# Revit family: ВУТ_ВУЕ ПБЕ_В_Л_П_Eng
name_source: partatom
category: Mechanical Equipment
units: mm (PartAtom-declared; Revit-internal decimal feet)

## family parameters
Always vertical = Yes
Classification = None
Cut with Voids When Loaded = No
Part Type = Normal
Room Calculation Point = No
Round Connector Dimension = Use Diameter
Shared = No
Work Plane-Based = No

## types (24) — shared parameters
00_20_Manufacturer = Vents
00_20_Name = Air handling units with heat recovery
Casing Material = Steel, galvanized
Filter = G4
Frequency = 50 Hz
Load Classification = HVAC
Maintenance zone material = <By Category>
Manufacturer = Vents
URL = https://ventilation-system.com
zero-valued in all types: Default Elevation

## per-type parameters (varying)
- VUE 300 PBE  ЕС L А21 DTV: 2000=No; 2000 PBV=No; Amperage=8 A; Apparent Load=1817 VA; B=485 mm; B3=135 mm  [stored 0.442913 ft]; B31=350 mm  [stored 1.14829 ft]; DW=12 mm  [stored 0.0393701 ft]; Diameter=160 mm  [stored 0.524934 ft]; Dn=155 mm  [stored 0.50853 ft]; Dy=160 mm  [stored 0.524934 ft]; EB=510 mm; EB1=268 mm  [stored 0.879265 ft]; EB2=50 mm  [stored 0.164042 ft]; H=280 mm  [stored 0.918635 ft]; H1=129 mm  [stored 0.423228 ft]; H2=590 mm; HW1=120 mm  [stored 0.393701 ft]; HW2=273 mm; Height=280 mm  [stored 0.918635 ft]; L=1238 mm; L1=1291 mm; LW1=254 mm; LW2=219 mm; Left=Yes; Left PBV=No; Left preostat=Yes; Length=1291 mm; Maximum Air Flow=340.0 m³/h; Number of Fase=1; Power=1680 W; Right=No; Right PBV=No; Sound pressure level at 3 m distance=27 dBA; Voltage=230 V; Weight=44.00 kg; Width=485 mm; b=243 mm
- VUT 300 PBE  ЕС L А21 DTV: 2000=No; 2000 PBV=No; Amperage=8 A; Apparent Load=1817 VA; B=485 mm; B3=135 mm  [stored 0.442913 ft]; B31=350 mm  [stored 1.14829 ft]; DW=12 mm  [stored 0.0393701 ft]; Diameter=160 mm  [stored 0.524934 ft]; Dn=155 mm  [stored 0.50853 ft]; Dy=160 mm  [stored 0.524934 ft]; EB=510 mm; EB1=268 mm  [stored 0.879265 ft]; EB2=50 mm  [stored 0.164042 ft]; H=280 mm  [stored 0.918635 ft]; H1=129 mm  [stored 0.423228 ft]; H2=590 mm; HW1=120 mm  [stored 0.393701 ft]; HW2=273 mm; Height=280 mm  [stored 0.918635 ft]; L=1238 mm; L1=1291 mm; LW1=254 mm; LW2=219 mm; Left=Yes; Left PBV=No; Left preostat=Yes; Length=1291 mm; Maximum Air Flow=340.0 m³/h; Number of Fase=1; Power=1680 W; Right=No; Right PBV=No; Sound pressure level at 3 m distance=27 dBA; Voltage=230 V; Weight=44.00 kg; Width=485 mm; b=243 mm
- VUE 300 PBE  ЕС R А21 DTV: 2000=No; 2000 PBV=No; Amperage=8 A; Apparent Load=1817 VA; B=485 mm; B3=350 mm  [stored 1.14829 ft]; B31=135 mm  [stored 0.442913 ft]; DW=12 mm  [stored 0.0393701 ft]; Diameter=160 mm  [stored 0.524934 ft]; Dn=155 mm  [stored 0.50853 ft]; Dy=160 mm  [stored 0.524934 ft]; EB=510 mm; EB1=268 mm  [stored 0.879265 ft]; EB2=50 mm  [stored 0.164042 ft]; H=280 mm  [stored 0.918635 ft]; H1=129 mm  [stored 0.423228 ft]; H2=590 mm; HW1=120 mm  [stored 0.393701 ft]; HW2=273 mm; Height=280 mm  [stored 0.918635 ft]; L=1238 mm; L1=1291 mm; LW1=254 mm; LW2=219 mm; Left=No; Left PBV=No; Left preostat=Yes; Length=1291 mm; Maximum Air Flow=340.0 m³/h; Number of Fase=1; Power=1680 W; Right=Yes; Right PBV=No; Sound pressure level at 3 m distance=27 dBA; Voltage=230 V; Weight=44.00 kg; Width=485 mm; b=243 mm
- VUT 300 PBE  ЕС R А21 DTV: 2000=No; 2000 PBV=No; Amperage=8 A; Apparent Load=1817 VA; B=485 mm; B3=350 mm  [stored 1.14829 ft]; B31=135 mm  [stored 0.442913 ft]; DW=12 mm  [stored 0.0393701 ft]; Diameter=160 mm  [stored 0.524934 ft]; Dn=155 mm  [stored 0.50853 ft]; Dy=160 mm  [stored 0.524934 ft]; EB=510 mm; EB1=268 mm  [stored 0.879265 ft]; EB2=50 mm  [stored 0.164042 ft]; H=280 mm  [stored 0.918635 ft]; H1=129 mm  [stored 0.423228 ft]; H2=590 mm; HW1=120 mm  [stored 0.393701 ft]; HW2=273 mm; Height=280 mm  [stored 0.918635 ft]; L=1238 mm; L1=1291 mm; LW1=254 mm; LW2=219 mm; Left=No; Left PBV=No; Left preostat=Yes; Length=1291 mm; Maximum Air Flow=340.0 m³/h; Number of Fase=1; Power=1680 W; Right=Yes; Right PBV=No; Sound pressure level at 3 m distance=27 dBA; Voltage=230 V; Weight=44.00 kg; Width=485 mm; b=243 mm
- VUE 550 PBE  ЕС L А21 DTV: 2000=No; 2000 PBV=No; Amperage=11 A; Apparent Load=2553 VA; B=827 mm; B3=188 mm  [stored 0.616798 ft]; B31=639 mm; DW=12 mm  [stored 0.0393701 ft]; Diameter=200 mm  [stored 0.656168 ft]; Dn=195 mm  [stored 0.639764 ft]; Dy=200 mm  [stored 0.656168 ft]; EB=802 mm; EB1=389 mm; EB2=5 mm  [stored 0.0164042 ft]; H=280 mm  [stored 0.918635 ft]; H1=120 mm  [stored 0.393701 ft]; H2=590 mm; HW1=160 mm  [stored 0.524934 ft]; HW2=250 mm  [stored 0.82021 ft]; Height=280 mm  [stored 0.918635 ft]; L=1238 mm; L1=1291 mm; LW1=350 mm  [stored 1.14829 ft]; LW2=370 mm  [stored 1.21391 ft]; Left=Yes; Left PBV=No; Left preostat=Yes; Length=1291 mm; Maximum Air Flow=620.0 m³/h; Number of Fase=1; Power=2297 W; Right=No; Right PBV=No; Sound pressure level at 3 m distance=30 dBA; Voltage=230 V; Weight=67.00 kg; Width=827 mm; b=414 mm
- VUE 550 PBE  ЕС R А21 DTV: 2000=No; 2000 PBV=No; Amperage=11 A; Apparent Load=2553 VA; B=827 mm; B3=188 mm  [stored 0.616798 ft]; B31=639 mm; DW=12 mm  [stored 0.0393701 ft]; Diameter=200 mm  [stored 0.656168 ft]; Dn=195 mm  [stored 0.639764 ft]; Dy=200 mm  [stored 0.656168 ft]; EB=802 mm; EB1=389 mm; EB2=5 mm  [stored 0.0164042 ft]; H=280 mm  [stored 0.918635 ft]; H1=120 mm  [stored 0.393701 ft]; H2=590 mm; HW1=160 mm  [stored 0.524934 ft]; HW2=250 mm  [stored 0.82021 ft]; Height=280 mm  [stored 0.918635 ft]; L=1238 mm; L1=1291 mm; LW1=350 mm  [stored 1.14829 ft]; LW2=370 mm  [stored 1.21391 ft]; Left=No; Left PBV=No; Left preostat=Yes; Length=1291 mm; Maximum Air Flow=620.0 m³/h; Number of Fase=1; Power=2297 W; Right=Yes; Right PBV=No; Sound pressure level at 3 m distance=30 dBA; Voltage=230 V; Weight=67.00 kg; Width=827 mm; b=414 mm
- VUT 550 PBE  ЕС L А21 DTV: 2000=No; 2000 PBV=No; Amperage=11 A; Apparent Load=2553 VA; B=827 mm; B3=188 mm  [stored 0.616798 ft]; B31=639 mm; DW=12 mm  [stored 0.0393701 ft]; Diameter=200 mm  [stored 0.656168 ft]; Dn=195 mm  [stored 0.639764 ft]; Dy=200 mm  [stored 0.656168 ft]; EB=802 mm; EB1=389 mm; EB2=5 mm  [stored 0.0164042 ft]; H=280 mm  [stored 0.918635 ft]; H1=120 mm  [stored 0.393701 ft]; H2=590 mm; HW1=160 mm  [stored 0.524934 ft]; HW2=250 mm  [stored 0.82021 ft]; Height=280 mm  [stored 0.918635 ft]; L=1238 mm; L1=1291 mm; LW1=350 mm  [stored 1.14829 ft]; LW2=370 mm  [stored 1.21391 ft]; Left=Yes; Left PBV=No; Left preostat=Yes; Length=1291 mm; Maximum Air Flow=620.0 m³/h; Number of Fase=1; Power=2297 W; Right=No; Right PBV=No; Sound pressure level at 3 m distance=30 dBA; Voltage=230 V; Weight=67.00 kg; Width=827 mm; b=414 mm
- VUT 550 PBE  ЕС R А21 DTV: 2000=No; 2000 PBV=No; Amperage=11 A; Apparent Load=2553 VA; B=827 mm; B3=188 mm  [stored 0.616798 ft]; B31=639 mm; DW=12 mm  [stored 0.0393701 ft]; Diameter=200 mm  [stored 0.656168 ft]; Dn=195 mm  [stored 0.639764 ft]; Dy=200 mm  [stored 0.656168 ft]; EB=802 mm; EB1=389 mm; EB2=5 mm  [stored 0.0164042 ft]; H=280 mm  [stored 0.918635 ft]; H1=120 mm  [stored 0.393701 ft]; H2=590 mm; HW1=160 mm  [stored 0.524934 ft]; HW2=250 mm  [stored 0.82021 ft]; Height=280 mm  [stored 0.918635 ft]; L=1238 mm; L1=1291 mm; LW1=350 mm  [stored 1.14829 ft]; LW2=370 mm  [stored 1.21391 ft]; Left=No; Left PBV=No; Left preostat=Yes; Length=1291 mm; Maximum Air Flow=620.0 m³/h; Number of Fase=1; Power=2297 W; Right=Yes; Right PBV=No; Sound pressure level at 3 m distance=30 dBA; Voltage=230 V; Weight=67.00 kg; Width=827 mm; b=414 mm
- VUE 900 PBE  ЕС L А21 DTV: 2000=No; 2000 PBV=No; Amperage=17 A; Apparent Load=4002 VA; B=1351 mm; B3=350 mm  [stored 1.14829 ft]; B31=1080 mm; DW=20 mm  [stored 0.0656168 ft]; Diameter=250 mm  [stored 0.82021 ft]; Dn=245 mm  [stored 0.803806 ft]; Dy=250 mm  [stored 0.82021 ft]; EB=1326 mm; EB1=651 mm; EB2=5 mm  [stored 0.0164042 ft]; H=318 mm  [stored 1.04331 ft]; H1=143 mm; H2=590 mm; HW1=50 mm  [stored 0.164042 ft]; HW2=265 mm  [stored 0.869423 ft]; Height=318 mm  [stored 1.04331 ft]; L=1349 mm; L1=1402 mm; LW1=70 mm  [stored 0.229659 ft]; LW2=135 mm  [stored 0.442913 ft]; Left=Yes; Left PBV=No; Left preostat=Yes; Length=1402 mm; Maximum Air Flow=1030.0 m³/h; Number of Fase=1; Power=3742 W; Right=No; Right PBV=No; Sound pressure level at 3 m distance=33 dBA; Voltage=230 V; Weight=111.00 kg; Width=1351 mm; b=676 mm
- VUE 900 PBE  ЕС R А21 DTV: 2000=No; 2000 PBV=No; Amperage=17 A; Apparent Load=4002 VA; B=1351 mm; B3=430 mm; B31=1080 mm; DW=20 mm  [stored 0.0656168 ft]; Diameter=250 mm  [stored 0.82021 ft]; Dn=245 mm  [stored 0.803806 ft]; Dy=250 mm  [stored 0.82021 ft]; EB=1326 mm; EB1=651 mm; EB2=5 mm  [stored 0.0164042 ft]; H=318 mm  [stored 1.04331 ft]; H1=143 mm; H2=590 mm; HW1=50 mm  [stored 0.164042 ft]; HW2=265 mm  [stored 0.869423 ft]; Height=318 mm  [stored 1.04331 ft]; L=1349 mm; L1=1402 mm; LW1=70 mm  [stored 0.229659 ft]; LW2=135 mm  [stored 0.442913 ft]; Left=No; Left PBV=No; Left preostat=Yes; Length=1402 mm; Maximum Air Flow=1030.0 m³/h; Number of Fase=1; Power=3742 W; Right=Yes; Right PBV=No; Sound pressure level at 3 m distance=33 dBA; Voltage=230 V; Weight=111.00 kg; Width=1351 mm; b=676 mm
- VUT 900 PBE  ЕС L А21 DTV: 2000=No; 2000 PBV=No; Amperage=17 A; Apparent Load=4002 VA; B=1351 mm; B3=350 mm  [stored 1.14829 ft]; B31=1080 mm; DW=20 mm  [stored 0.0656168 ft]; Diameter=250 mm  [stored 0.82021 ft]; Dn=245 mm  [stored 0.803806 ft]; Dy=250 mm  [stored 0.82021 ft]; EB=1326 mm; EB1=651 mm; EB2=5 mm  [stored 0.0164042 ft]; H=318 mm  [stored 1.04331 ft]; H1=143 mm; H2=590 mm; HW1=50 mm  [stored 0.164042 ft]; HW2=265 mm  [stored 0.869423 ft]; Height=318 mm  [stored 1.04331 ft]; L=1349 mm; L1=1402 mm; LW1=70 mm  [stored 0.229659 ft]; LW2=135 mm  [stored 0.442913 ft]; Left=Yes; Left PBV=No; Left preostat=Yes; Length=1402 mm; Maximum Air Flow=1030.0 m³/h; Number of Fase=1; Power=3742 W; Right=No; Right PBV=No; Sound pressure level at 3 m distance=33 dBA; Voltage=230 V; Weight=111.00 kg; Width=1351 mm; b=676 mm
- VUT 900 PBE  ЕС R А21 DTV: 2000=No; 2000 PBV=No; Amperage=17 A; Apparent Load=4002 VA; B=1351 mm; B3=430 mm; B31=1080 mm; DW=20 mm  [stored 0.0656168 ft]; Diameter=250 mm  [stored 0.82021 ft]; Dn=245 mm  [stored 0.803806 ft]; Dy=250 mm  [stored 0.82021 ft]; EB=1326 mm; EB1=651 mm; EB2=5 mm  [stored 0.0164042 ft]; H=318 mm  [stored 1.04331 ft]; H1=143 mm; H2=590 mm; HW1=50 mm  [stored 0.164042 ft]; HW2=265 mm  [stored 0.869423 ft]; Height=318 mm  [stored 1.04331 ft]; L=1349 mm; L1=1402 mm; LW1=70 mm  [stored 0.229659 ft]; LW2=135 mm  [stored 0.442913 ft]; Left=No; Left PBV=No; Left preostat=Yes; Length=1402 mm; Maximum Air Flow=1030.0 m³/h; Number of Fase=1; Power=3742 W; Right=Yes; Right PBV=No; Sound pressure level at 3 m distance=33 dBA; Voltage=230 V; Weight=111.00 kg; Width=1351 mm; b=676 mm
- VUE 550 PBW ЕС L А21 DTV: 2000=No; 2000 PBV=No; Amperage=2 A; Apparent Load=552 VA; B=827 mm; B3=188 mm  [stored 0.616798 ft]; B31=639 mm; DW=12 mm  [stored 0.0393701 ft]; Diameter=200 mm  [stored 0.656168 ft]; Dn=195 mm  [stored 0.639764 ft]; Dy=200 mm  [stored 0.656168 ft]; EB=802 mm; EB1=389 mm; EB2=5 mm  [stored 0.0164042 ft]; H=280 mm  [stored 0.918635 ft]; H1=120 mm  [stored 0.393701 ft]; H2=590 mm; HW1=160 mm  [stored 0.524934 ft]; HW2=250 mm  [stored 0.82021 ft]; Height=280 mm  [stored 0.918635 ft]; L=1238 mm; L1=1291 mm; LW1=350 mm  [stored 1.14829 ft]; LW2=370 mm  [stored 1.21391 ft]; Left=Yes; Left PBV=Yes; Left preostat=Yes; Length=1291 mm; Maximum Air Flow=620.0 m³/h; Number of Fase=1; Power=297 W; Right=No; Right PBV=No; Sound pressure level at 3 m distance=30 dBA; Voltage=230 V; Weight=68.00 kg; Width=827 mm; b=414 mm
- VUT 550 PBW ЕС L А21 DTV: 2000=No; 2000 PBV=No; Amperage=2 A; Apparent Load=552 VA; B=827 mm; B3=188 mm  [stored 0.616798 ft]; B31=639 mm; DW=12 mm  [stored 0.0393701 ft]; Diameter=200 mm  [stored 0.656168 ft]; Dn=195 mm  [stored 0.639764 ft]; Dy=200 mm  [stored 0.656168 ft]; EB=802 mm; EB1=389 mm; EB2=5 mm  [stored 0.0164042 ft]; H=280 mm  [stored 0.918635 ft]; H1=120 mm  [stored 0.393701 ft]; H2=590 mm; HW1=160 mm  [stored 0.524934 ft]; HW2=250 mm  [stored 0.82021 ft]; Height=280 mm  [stored 0.918635 ft]; L=1238 mm; L1=1291 mm; LW1=350 mm  [stored 1.14829 ft]; LW2=370 mm  [stored 1.21391 ft]; Left=Yes; Left PBV=Yes; Left preostat=Yes; Length=1291 mm; Maximum Air Flow=620.0 m³/h; Number of Fase=1; Power=297 W; Right=No; Right PBV=No; Sound pressure level at 3 m distance=30 dBA; Voltage=230 V; Weight=68.00 kg; Width=827 mm; b=414 mm
- VUE 550 PBW ЕС R А21 DTV: 2000=No; 2000 PBV=No; Amperage=2 A; Apparent Load=552 VA; B=827 mm; B3=188 mm  [stored 0.616798 ft]; B31=639 mm; DW=12 mm  [stored 0.0393701 ft]; Diameter=200 mm  [stored 0.656168 ft]; Dn=195 mm  [stored 0.639764 ft]; Dy=200 mm  [stored 0.656168 ft]; EB=802 mm; EB1=389 mm; EB2=5 mm  [stored 0.0164042 ft]; H=280 mm  [stored 0.918635 ft]; H1=120 mm  [stored 0.393701 ft]; H2=590 mm; HW1=160 mm  [stored 0.524934 ft]; HW2=250 mm  [stored 0.82021 ft]; Height=280 mm  [stored 0.918635 ft]; L=1238 mm; L1=1291 mm; LW1=350 mm  [stored 1.14829 ft]; LW2=370 mm  [stored 1.21391 ft]; Left=No; Left PBV=No; Left preostat=Yes; Length=1291 mm; Maximum Air Flow=620.0 m³/h; Number of Fase=1; Power=297 W; Right=Yes; Right PBV=Yes; Sound pressure level at 3 m distance=30 dBA; Voltage=230 V; Weight=68.00 kg; Width=827 mm; b=414 mm
- VUT 550 PBW ЕС R А21 DTV: 2000=No; 2000 PBV=No; Amperage=2 A; Apparent Load=552 VA; B=827 mm; B3=188 mm  [stored 0.616798 ft]; B31=639 mm; DW=12 mm  [stored 0.0393701 ft]; Diameter=200 mm  [stored 0.656168 ft]; Dn=195 mm  [stored 0.639764 ft]; Dy=200 mm  [stored 0.656168 ft]; EB=802 mm; EB1=389 mm; EB2=5 mm  [stored 0.0164042 ft]; H=280 mm  [stored 0.918635 ft]; H1=120 mm  [stored 0.393701 ft]; H2=590 mm; HW1=160 mm  [stored 0.524934 ft]; HW2=250 mm  [stored 0.82021 ft]; Height=280 mm  [stored 0.918635 ft]; L=1238 mm; L1=1291 mm; LW1=350 mm  [stored 1.14829 ft]; LW2=370 mm  [stored 1.21391 ft]; Left=No; Left PBV=No; Left preostat=Yes; Length=1291 mm; Maximum Air Flow=620.0 m³/h; Number of Fase=1; Power=297 W; Right=Yes; Right PBV=Yes; Sound pressure level at 3 m distance=30 dBA; Voltage=230 V; Weight=68.00 kg; Width=827 mm; b=414 mm
- VUE 900 PBW ЕС L А21 DTV: 2000=No; 2000 PBV=No; Amperage=3 A; Apparent Load=690 VA; B=1351 mm; B3=350 mm  [stored 1.14829 ft]; B31=1080 mm; DW=20 mm  [stored 0.0656168 ft]; Diameter=250 mm  [stored 0.82021 ft]; Dn=245 mm  [stored 0.803806 ft]; Dy=250 mm  [stored 0.82021 ft]; EB=1326 mm; EB1=651 mm; EB2=5 mm  [stored 0.0164042 ft]; H=318 mm  [stored 1.04331 ft]; H1=143 mm; H2=590 mm; HW1=50 mm  [stored 0.164042 ft]; HW2=265 mm  [stored 0.869423 ft]; Height=318 mm  [stored 1.04331 ft]; L=1349 mm; L1=1402 mm; LW1=70 mm  [stored 0.229659 ft]; LW2=135 mm  [stored 0.442913 ft]; Left=Yes; Left PBV=Yes; Left preostat=Yes; Length=1402 mm; Maximum Air Flow=1030.0 m³/h; Number of Fase=1; Power=442 W; Right=No; Right PBV=No; Sound pressure level at 3 m distance=33 dBA; Voltage=230 V; Weight=112.00 kg; Width=1351 mm; b=676 mm
- VUT 900 PBW ЕС L А21 DTV: 2000=No; 2000 PBV=No; Amperage=3 A; Apparent Load=690 VA; B=1351 mm; B3=350 mm  [stored 1.14829 ft]; B31=1080 mm; DW=20 mm  [stored 0.0656168 ft]; Diameter=250 mm  [stored 0.82021 ft]; Dn=245 mm  [stored 0.803806 ft]; Dy=250 mm  [stored 0.82021 ft]; EB=1326 mm; EB1=651 mm; EB2=5 mm  [stored 0.0164042 ft]; H=318 mm  [stored 1.04331 ft]; H1=143 mm; H2=590 mm; HW1=50 mm  [stored 0.164042 ft]; HW2=265 mm  [stored 0.869423 ft]; Height=318 mm  [stored 1.04331 ft]; L=1349 mm; L1=1402 mm; LW1=70 mm  [stored 0.229659 ft]; LW2=135 mm  [stored 0.442913 ft]; Left=Yes; Left PBV=Yes; Left preostat=Yes; Length=1402 mm; Maximum Air Flow=1030.0 m³/h; Number of Fase=1; Power=442 W; Right=No; Right PBV=No; Sound pressure level at 3 m distance=33 dBA; Voltage=230 V; Weight=112.00 kg; Width=1351 mm; b=676 mm
- VUE 900 PBW ЕС R А21 DTV: 2000=No; 2000 PBV=No; Amperage=3 A; Apparent Load=690 VA; B=1351 mm; B3=430 mm; B31=1080 mm; DW=20 mm  [stored 0.0656168 ft]; Diameter=250 mm  [stored 0.82021 ft]; Dn=245 mm  [stored 0.803806 ft]; Dy=250 mm  [stored 0.82021 ft]; EB=1326 mm; EB1=651 mm; EB2=5 mm  [stored 0.0164042 ft]; H=318 mm  [stored 1.04331 ft]; H1=143 mm; H2=590 mm; HW1=50 mm  [stored 0.164042 ft]; HW2=265 mm  [stored 0.869423 ft]; Height=318 mm  [stored 1.04331 ft]; L=1349 mm; L1=1402 mm; LW1=70 mm  [stored 0.229659 ft]; LW2=135 mm  [stored 0.442913 ft]; Left=No; Left PBV=No; Left preostat=Yes; Length=1402 mm; Maximum Air Flow=1030.0 m³/h; Number of Fase=1; Power=442 W; Right=Yes; Right PBV=Yes; Sound pressure level at 3 m distance=33 dBA; Voltage=230 V; Weight=112.00 kg; Width=1351 mm; b=676 mm
- VUT 900 PBW ЕС R А21 DTV: 2000=No; 2000 PBV=No; Amperage=3 A; Apparent Load=690 VA; B=1351 mm; B3=430 mm; B31=1080 mm; DW=20 mm  [stored 0.0656168 ft]; Diameter=250 mm  [stored 0.82021 ft]; Dn=245 mm  [stored 0.803806 ft]; Dy=250 mm  [stored 0.82021 ft]; EB=1326 mm; EB1=651 mm; EB2=5 mm  [stored 0.0164042 ft]; H=318 mm  [stored 1.04331 ft]; H1=143 mm; H2=590 mm; HW1=50 mm  [stored 0.164042 ft]; HW2=265 mm  [stored 0.869423 ft]; Height=318 mm  [stored 1.04331 ft]; L=1349 mm; L1=1402 mm; LW1=70 mm  [stored 0.229659 ft]; LW2=135 mm  [stored 0.442913 ft]; Left=No; Left PBV=No; Left preostat=Yes; Length=1402 mm; Maximum Air Flow=1030.0 m³/h; Number of Fase=1; Power=442 W; Right=Yes; Right PBV=Yes; Sound pressure level at 3 m distance=33 dBA; Voltage=230 V; Weight=112.00 kg; Width=1351 mm; b=676 mm
- VUT 2000 PBE  ЕС А21 DTV: 2000=Yes; 2000 PBV=No; Amperage=27 A; Apparent Load=10800 VA; B=950 mm; B3=225 mm  [stored 0.738189 ft]; B31=725 mm; DW=20 mm  [stored 0.0656168 ft]; Diameter=315 mm  [stored 1.03346 ft]; Dn=310 mm  [stored 1.01706 ft]; Dy=315 mm  [stored 1.03346 ft]; EB=925 mm; EB1=450 mm  [stored 1.47638 ft]; EB2=5 mm  [stored 0.0164042 ft]; H=762 mm; H1=367 mm  [stored 1.20407 ft]; H2=690 mm; HW1=50 mm  [stored 0.164042 ft]; HW2=265 mm  [stored 0.869423 ft]; Height=762 mm; L=1400 mm; L1=1453 mm; LW1=70 mm  [stored 0.229659 ft]; LW2=135 mm  [stored 0.442913 ft]; Left=Yes; Left PBV=No; Left preostat=No; Length=1453 mm; Maximum Air Flow=2100.0 m³/h; Number of Fase=3; Power=15876 W; Right=No; Right PBV=No; Sound pressure level at 3 m distance=36 dBA; Voltage=400 V; Weight=140.00 kg; Width=950 mm; b=475 mm  [stored 1.5584 ft]
- VUT 3000 PBE  ЕС А21 DTV: 2000=Yes; 2000 PBV=No; Amperage=34 A; Apparent Load=13400 VA; B=1265 mm; B3=347 mm  [stored 1.13845 ft]; B31=918 mm; DW=20 mm  [stored 0.0656168 ft]; Diameter=400 mm  [stored 1.31234 ft]; Dn=395 mm  [stored 1.29593 ft]; Dy=400 mm  [stored 1.31234 ft]; EB=1240 mm; EB1=608 mm; EB2=5 mm  [stored 0.0164042 ft]; H=881 mm; H1=427 mm  [stored 1.40092 ft]; H2=590 mm; HW1=50 mm  [stored 0.164042 ft]; HW2=265 mm  [stored 0.869423 ft]; Height=881 mm; L=1835 mm; L1=1888 mm; LW1=70 mm  [stored 0.229659 ft]; LW2=135 mm  [stored 0.442913 ft]; Left=Yes; Left PBV=No; Left preostat=No; Length=1888 mm; Maximum Air Flow=4300.0 m³/h; Number of Fase=3; Power=23226 W; Right=No; Right PBV=No; Sound pressure level at 3 m distance=46 dBA; Voltage=400 V; Weight=281.00 kg; Width=1265 mm; b=633 mm
- VUT 2000 PBW ЕС А21 DTV: 2000=Yes; 2000 PBV=Yes; Amperage=5 A; Apparent Load=1219 VA; B=950 mm; B3=225 mm  [stored 0.738189 ft]; B31=725 mm; DW=20 mm  [stored 0.0656168 ft]; Diameter=315 mm  [stored 1.03346 ft]; Dn=310 mm  [stored 1.01706 ft]; Dy=315 mm  [stored 1.03346 ft]; EB=925 mm; EB1=450 mm  [stored 1.47638 ft]; EB2=5 mm  [stored 0.0164042 ft]; H=762 mm; H1=367 mm  [stored 1.20407 ft]; H2=690 mm; HW1=50 mm  [stored 0.164042 ft]; HW2=265 mm  [stored 0.869423 ft]; Height=762 mm; L=1400 mm; L1=1453 mm; LW1=70 mm  [stored 0.229659 ft]; LW2=135 mm  [stored 0.442913 ft]; Left=Yes; Left PBV=No; Left preostat=No; Length=1453 mm; Maximum Air Flow=2100.0 m³/h; Number of Fase=1; Power=876 W; Right=No; Right PBV=No; Sound pressure level at 3 m distance=36 dBA; Voltage=230 V; Weight=140.00 kg; Width=950 mm; b=475 mm  [stored 1.5584 ft]
- VUT 3000 PBW ЕС А21 DTV: 2000=Yes; 2000 PBV=Yes; Amperage=4 A; Apparent Load=1400 VA; B=1265 mm; B3=347 mm  [stored 1.13845 ft]; B31=918 mm; DW=20 mm  [stored 0.0656168 ft]; Diameter=400 mm  [stored 1.31234 ft]; Dn=395 mm  [stored 1.29593 ft]; Dy=400 mm  [stored 1.31234 ft]; EB=1240 mm; EB1=608 mm; EB2=5 mm  [stored 0.0164042 ft]; H=881 mm; H1=427 mm  [stored 1.40092 ft]; H2=590 mm; HW1=50 mm  [stored 0.164042 ft]; HW2=265 mm  [stored 0.869423 ft]; Height=881 mm; L=1835 mm; L1=1888 mm; LW1=70 mm  [stored 0.229659 ft]; LW2=135 mm  [stored 0.442913 ft]; Left=Yes; Left PBV=No; Left preostat=No; Length=1888 mm; Maximum Air Flow=4300.0 m³/h; Number of Fase=3; Power=2226 W; Right=No; Right PBV=No; Sound pressure level at 3 m distance=46 dBA; Voltage=400 V; Weight=268.00 kg; Width=1265 mm; b=633 mm

note: column(s) folded — value = type name in every type: 00_20_Type

note: [stored X ft] marks values corroborated as IEEE doubles in the binary element streams (Revit-internal decimal feet)
